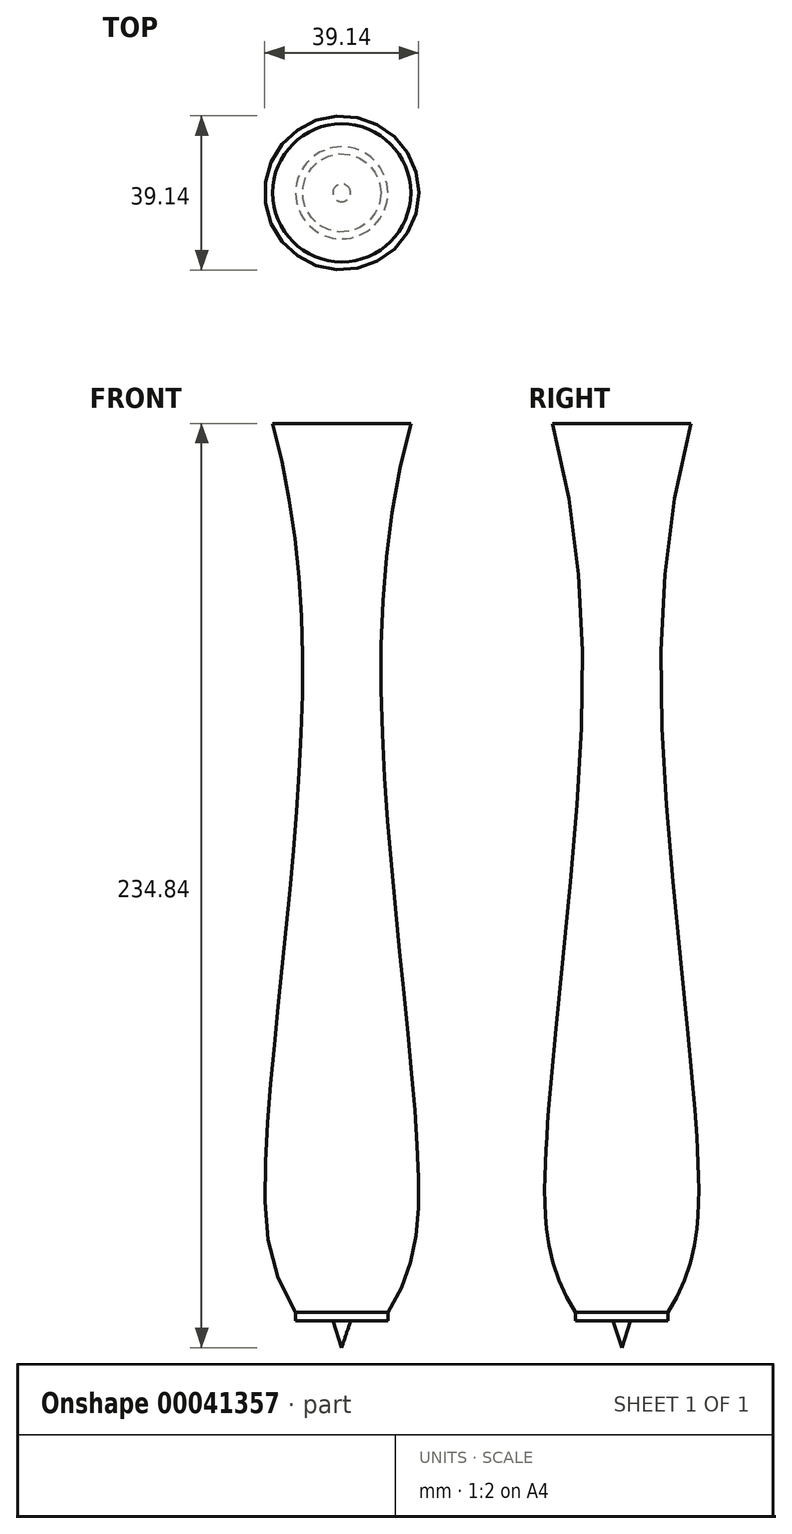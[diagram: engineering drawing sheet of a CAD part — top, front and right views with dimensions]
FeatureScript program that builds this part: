
annotation { "Feature Type Name" : "Feature", "Feature Type Description" : "" }
export const myFeature = defineFeature(function(context is Context, id is Id, definition is map)
    precondition{}
    {
        {
            var Q0;
            Q0=qCreatedBy(makeId("Front.planeOp"),FACE);
            var sketch = newSketch(context, id + "F0", { "sketchPlane" : qUnion([Q0])});
            skLineSegment(sketch, "E0", {"start": v(0, 0) * mm, "end": v(-2.27, 6.8) * mm});
            skLineSegment(sketch, "E1", {"start": v(-2.27, 6.8) * mm, "end": v(-11.7, 6.8) * mm});
            skLineSegment(sketch, "E2", {"start": v(-11.7, 6.8) * mm, "end": v(-11.7, 8.92) * mm});
            skFitSpline(sketch, "E3", {"points": [v(-11.7, 8.92) * mm, v(-19.3, 49.12) * mm, v(-11.7, 133.5) * mm, v(-17.55, 234.84) * mm], "startDerivative": vector(-94.06, 142.64) * mm, "endDerivative": vector(-70.21, 262.04) * mm});
            skLineSegment(sketch, "E4", {"start": v(-17.55, 234.84) * mm, "end": v(0, 234.84) * mm});
            skLineSegment(sketch, "E5", {"start": v(0, 234.84) * mm, "end": v(0, 0) * mm});
            skSolve(sketch);
        }
        {
            var Q0;
            Q0=makeQuery(id+"F0.imprint","IMPRINT",FACE,{"disambiguationData":[TD([[makeQuery(id+"F0.imprint","IMPRINT",EDGE,{"derivedFrom":sQuery(id+"F0.wireOp",EDGE,"E0")}),-1.0]])]});
            var Q1;
            Q1=sQuery(id+"F0.wireOp",EDGE,"E5");
            revolve(context, id + "F1", {"entities" : qUnion([Q0]), "axis" : qUnion([Q1]), "revolveType" : RevolveType.FULL});
        }
    });
